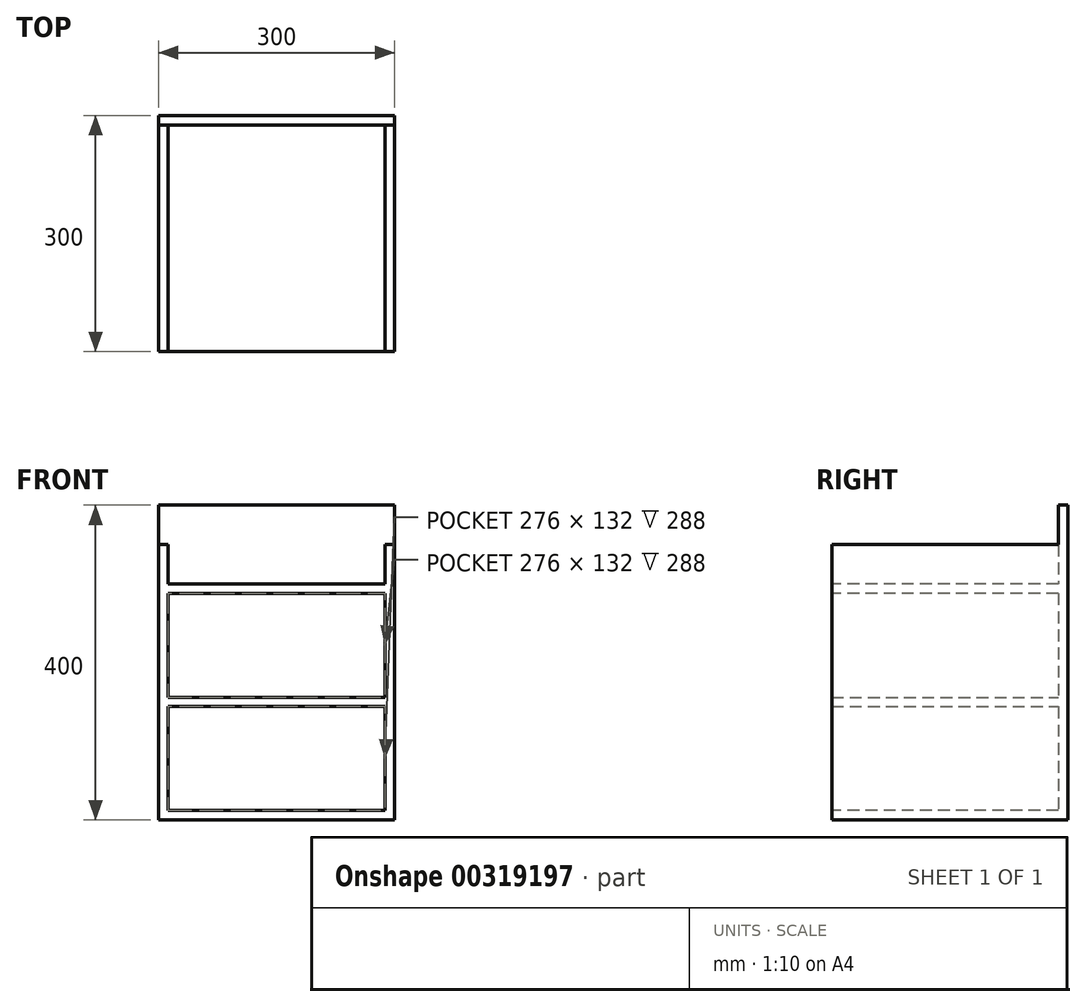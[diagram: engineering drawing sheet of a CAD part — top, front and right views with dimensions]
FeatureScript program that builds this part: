
annotation { "Feature Type Name" : "Feature", "Feature Type Description" : "" }
export const myFeature = defineFeature(function(context is Context, id is Id, definition is map)
    precondition{}
    {
        {
            var Q0;
            Q0=qCreatedBy(makeId("Front.planeOp"),FACE);
            var sketch = newSketch(context, id + "F0", { "sketchPlane" : qUnion([Q0])});
            skLineSegment(sketch, "E0.bottom", {"start": v(-150, 150) * mm, "end": v(150, 150) * mm});
            skLineSegment(sketch, "E0.top", {"start": v(-150, -150) * mm, "end": v(150, -150) * mm});
            skLineSegment(sketch, "E0.left", {"start": v(-150, 150) * mm, "end": v(-150, -150) * mm});
            skLineSegment(sketch, "E0.right", {"start": v(150, 150) * mm, "end": v(150, -150) * mm});
            skPoint(sketch, "E0.middle", {"position": v(0, 0) * mm});
            skSolve(sketch);
        }
        {
            var Q0;
            Q0=makeQuery(id+"F0.imprint","IMPRINT",FACE,{"disambiguationData":[TD([[makeQuery(id+"F0.imprint","IMPRINT",EDGE,{"derivedFrom":sQuery(id+"F0.wireOp",EDGE,"E0.bottom")}),-1.0]])]});
            extrude(context, id + "F1", {"entities" : qUnion([Q0]), "oppositeDirection" : true, "depth" : 300 * mm});
        }
        {
            var Q0;
            Q0=makeQuery(id+"F1.opExtrude","CAP_FACE",FACE,{"disambiguationData":[OSD([sQuery(id+"F0.wireOp",EDGE,"E0.bottom"),sQuery(id+"F0.wireOp",EDGE,"E0.top"),sQuery(id+"F0.wireOp",EDGE,"E0.left"),sQuery(id+"F0.wireOp",EDGE,"E0.right")])],"isStart":true});
            shell(context, id + "F2", {"entities" : qUnion([Q0]), "thickness" : 12 * mm});
        }
        {
            var Q0;
            Q0=makeQuery(id+"F2.opShell","OFFSET_FACE",FACE,{"disambiguationData":[OSD([sQuery(id+"F0.wireOp",EDGE,"E0.bottom"),sQuery(id+"F0.wireOp",EDGE,"E0.top"),sQuery(id+"F0.wireOp",EDGE,"E0.left"),sQuery(id+"F0.wireOp",EDGE,"E0.right")])]});
            var sketch = newSketch(context, id + "F3", { "sketchPlane" : qUnion([Q0])});
            skLineSegment(sketch, "E1.bottom", {"start": v(138, 6) * mm, "end": v(-138, 6) * mm});
            skLineSegment(sketch, "E1.top", {"start": v(138, -6) * mm, "end": v(-138, -6) * mm});
            skLineSegment(sketch, "E1.left", {"start": v(138, 6) * mm, "end": v(138, -6) * mm});
            skLineSegment(sketch, "E1.right", {"start": v(-138, 6) * mm, "end": v(-138, -6) * mm});
            skPoint(sketch, "E1.middle", {"position": v(0, 0) * mm});
            skSolve(sketch);
        }
        {
            var Q0;
            Q0=makeQuery(id+"F3.imprint","IMPRINT",FACE,{"disambiguationData":[TD([[makeQuery(id+"F3.imprint","IMPRINT",EDGE,{"derivedFrom":sQuery(id+"F3.wireOp",EDGE,"E1.bottom")}),1.0]])]});
            extrude(context, id + "F4", {"entities" : qUnion([Q0]), "operationType" : NewBodyOperationType.ADD, "depth" : 288 * mm});
        }
        {
            var Q0;
            Q0=makeQuery(id+"F1.opExtrude","SWEPT_FACE",FACE,{"disambiguationData":[OSD([sQuery(id+"F0.wireOp",EDGE,"E0.bottom")])]});
            var sketch = newSketch(context, id + "F5", { "sketchPlane" : qUnion([Q0])});
            skLineSegment(sketch, "E2.bottom", {"start": v(-150, 300) * mm, "end": v(150, 300) * mm});
            skLineSegment(sketch, "E2.top", {"start": v(-150, 288) * mm, "end": v(150, 288) * mm});
            skLineSegment(sketch, "E2.left", {"start": v(-150, 300) * mm, "end": v(-150, 288) * mm});
            skLineSegment(sketch, "E2.right", {"start": v(150, 300) * mm, "end": v(150, 288) * mm});
            skSolve(sketch);
        }
        {
            var Q0;
            Q0=makeQuery(id+"F5.imprint","IMPRINT",FACE,{"disambiguationData":[TD([[makeQuery(id+"F5.imprint","IMPRINT",EDGE,{"derivedFrom":sQuery(id+"F5.wireOp",EDGE,"E2.bottom")}),-1.0]])]});
            extrude(context, id + "F6", {"entities" : qUnion([Q0]), "operationType" : NewBodyOperationType.ADD, "depth" : 100 * mm});
        }
        {
            var Q0;
            Q0=makeQuery(id+"F1.opExtrude","SWEPT_FACE",FACE,{"disambiguationData":[OSD([sQuery(id+"F0.wireOp",EDGE,"E0.bottom")])]});
            var sketch = newSketch(context, id + "F7", { "sketchPlane" : qUnion([Q0])});
            skLineSegment(sketch, "E3.bottom", {"start": v(-150, 288) * mm, "end": v(-138, 288) * mm});
            skLineSegment(sketch, "E3.top", {"start": v(-150, 0) * mm, "end": v(-138, 0) * mm});
            skLineSegment(sketch, "E3.left", {"start": v(-150, 288) * mm, "end": v(-150, 0) * mm});
            skLineSegment(sketch, "E3.right", {"start": v(-138, 288) * mm, "end": v(-138, 0) * mm});
            skSolve(sketch);
        }
        {
            var Q0;
            Q0=makeQuery(id+"F7.imprint","IMPRINT",FACE,{"disambiguationData":[TD([[makeQuery(id+"F7.imprint","IMPRINT",EDGE,{"derivedFrom":sQuery(id+"F7.wireOp",EDGE,"E3.bottom")}),-1.0]])]});
            extrude(context, id + "F8", {"entities" : qUnion([Q0]), "operationType" : NewBodyOperationType.ADD, "depth" : 50 * mm});
        }
        {
            var Q0;
            Q0=makeQuery(id+"F1.opExtrude","SWEPT_FACE",FACE,{"disambiguationData":[OSD([sQuery(id+"F0.wireOp",EDGE,"E0.bottom")])]});
            var sketch = newSketch(context, id + "F9", { "sketchPlane" : qUnion([Q0])});
            skLineSegment(sketch, "E4.bottom", {"start": v(150, 288) * mm, "end": v(138, 288) * mm});
            skLineSegment(sketch, "E4.top", {"start": v(150, 0) * mm, "end": v(138, 0) * mm});
            skLineSegment(sketch, "E4.left", {"start": v(150, 288) * mm, "end": v(150, 0) * mm});
            skLineSegment(sketch, "E4.right", {"start": v(138, 288) * mm, "end": v(138, 0) * mm});
            skSolve(sketch);
        }
        {
            var Q0;
            Q0=makeQuery(id+"F9.imprint","IMPRINT",FACE,{"disambiguationData":[TD([[makeQuery(id+"F9.imprint","IMPRINT",EDGE,{"derivedFrom":sQuery(id+"F9.wireOp",EDGE,"E4.bottom")}),-1.0]])]});
            extrude(context, id + "F10", {"entities" : qUnion([Q0]), "operationType" : NewBodyOperationType.ADD, "depth" : 50 * mm});
        }
    });
